# Revit family: NAU_Naughtone_Stng_Pullman_DeskPod
name_source: partatom
category: Furniture
revit_build: Autodesk Revit 2018 (Build: 20170223_1515(x64)
units: mm (PartAtom-declared; Revit-internal decimal feet)

## family parameters
Always vertical = Yes
Cut with Voids When Loaded = No
OmniClass Number = 23.40.20.00
OmniClass Title = General Furniture and Specialties
Room Calculation Point = No
Shared = Yes
Work Plane-Based = No

## types (3) — shared parameters
Assembly Code = E2020200
AssetType = Movable
BIMObjectName = NAU_Naughtone_Seating_Pullman_DeskPod
Category = Pr_40_50_21 : Desks, tables and worktops
DurationUnit = year
ExpectedLife = 10
Features = Available in two version of tone fabric.
Finish = Fabric upholstery. Desk top available in black or white MFMDF; oak or walnut veneer; or Forbo Lino.
IfcExportAs = IfcFurnishingElementType
IfcExportType = DESK
Keynote = Pr_40_50_21
ManufacturerAddress = Knaresborough Tech Park, Manse Lane, Knaresborough, HG5 8LF
ManufacturerName = Naughtone
ManufacturerURL = www.naughtone.com
Material = Fabric, plywood frame, foam
NBSDescription = Tables
NBSReference = 45-35-86/327
Name = Seating_Pullman_DeskPod_Naughtone
NominalHeight = 1300 mm  [stored 4.26509 ft]
NumberOfChairs = 1
ProductInformation = www.naughtone.com/products/pullmanchair/
Shape = Rectangular
URL = www.naughtone.com
Uniclass2015Code = Pr_40_50_21
Uniclass2015Title = Desks, tables and worktops
Uniclass2015Version = Products v1.22
Version = 1
WarrantyDescription = Request warranty information from naughtone
WarrantyDurationLabor = 10
WarrantyDurationParts = 10
WarrantyDurationUnit = year
zero-valued in all types: WorksurfaceArea

## per-type parameters (varying)
| type | HasScreenLeft | HasScreenRight | IsLeftPlinth | IsRightPlinth | Model | ModelNumber | NominalLength | NominalWidth | Size |
| Pullman Desk Pod 1200 - Access Right | Yes | No | Yes | No | PULDPHRPL | PULDPHRPL | 1600 mm  [stored 5.24934 ft] | 1300 mm  [stored 4.26509 ft] | 1600 x 1300 x 1300 mm |
| Pullman Desk Pod 1200 - Access Left | No | Yes | No | Yes | PULDPHLPL | PULDPHLPL | 1600 mm  [stored 5.24934 ft] | 1300 mm  [stored 4.26509 ft] | 1600 x 1300 x 1300 mm |
| Pullman Desk 1200 | No | No | No | No | PULDHPL | PULDHPL | 1300 mm  [stored 4.26509 ft] | 710 mm | 1300 x 710 x 1300 mm |

note: column(s) folded — value = type name in every type: Description, ModelReference

note: [stored X ft] marks values corroborated as IEEE doubles in the binary element streams (Revit-internal decimal feet)

## geometry (parser evidence)
native form markers: Sweep x2
no freeform markers — native parametric forms only
